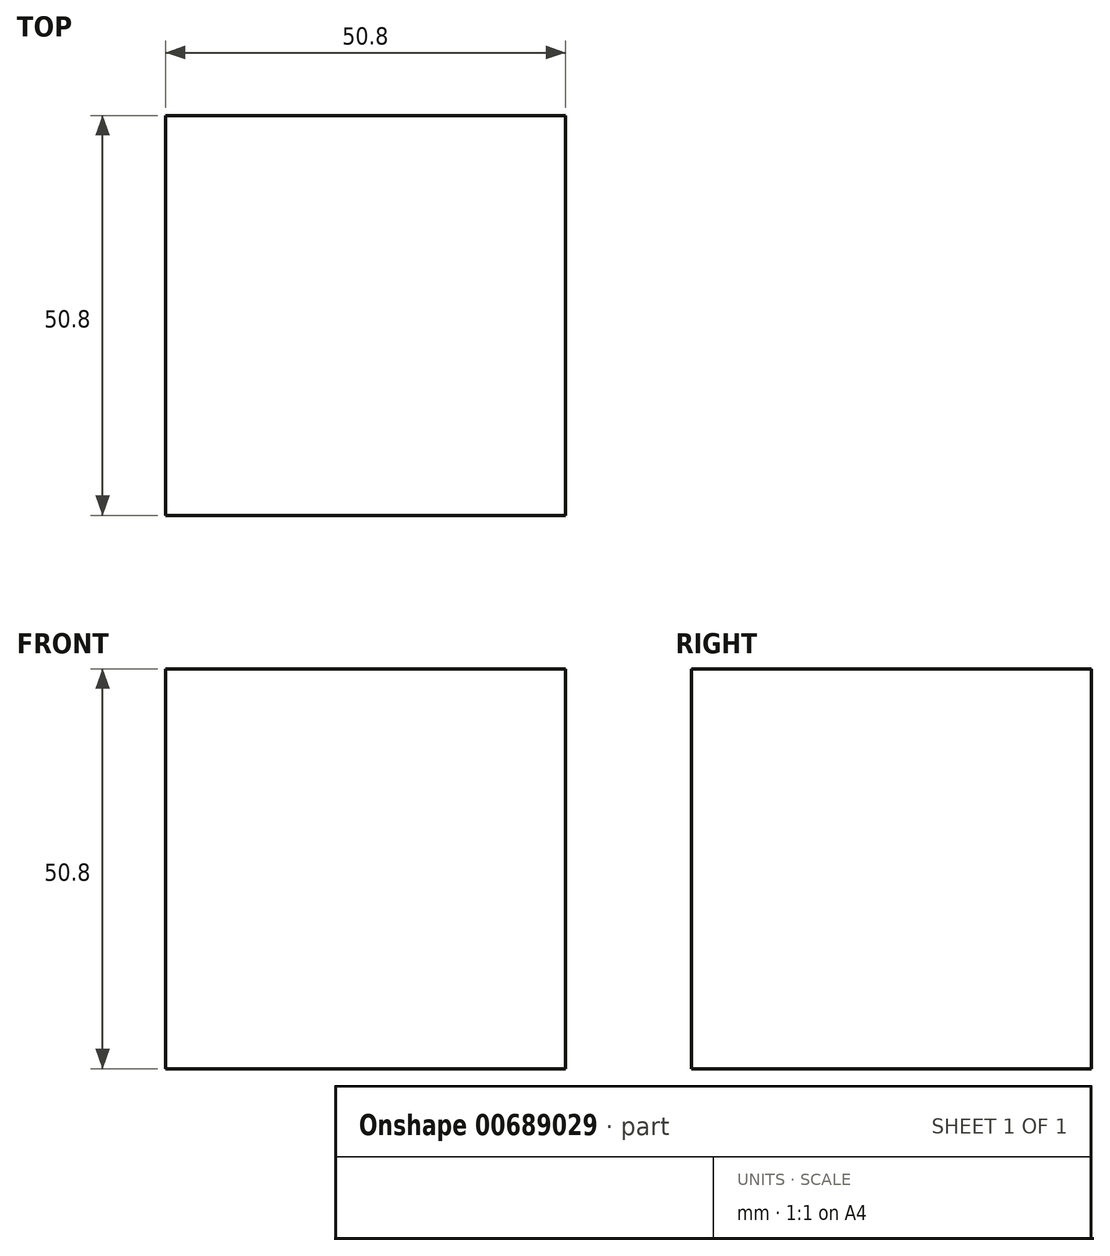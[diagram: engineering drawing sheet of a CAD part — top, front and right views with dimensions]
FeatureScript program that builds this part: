
annotation { "Feature Type Name" : "Feature", "Feature Type Description" : "" }
export const myFeature = defineFeature(function(context is Context, id is Id, definition is map)
    precondition{}
    {
        {
            var Q0;
            Q0=qCreatedBy(makeId("Front.planeOp"),FACE);
            var sketch = newSketch(context, id + "F0", { "sketchPlane" : qUnion([Q0])});
            skLineSegment(sketch, "E0", {"start": v(-61.96, 50.8) * mm, "end": v(-61.96, 0) * mm});
            skLineSegment(sketch, "E1", {"start": v(-61.96, 0) * mm, "end": v(-11.16, 0) * mm});
            skLineSegment(sketch, "E2", {"start": v(-11.16, 0) * mm, "end": v(-11.16, 50.8) * mm});
            skLineSegment(sketch, "E3", {"start": v(-11.16, 50.8) * mm, "end": v(-61.96, 50.8) * mm});
            skLineSegment(sketch, "E4", {"start": v(-61.96, 25.4) * mm, "end": v(-36.56, 25.4) * mm});
            skLineSegment(sketch, "E5", {"start": v(-36.56, 25.4) * mm, "end": v(-36.56, 0) * mm});
            skSolve(sketch);
        }
        {
            var Q0;
            {var subQ0=sQuery(id+"F0.wireOp",EDGE,"E2");Q0=makeQuery(id+"F0.imprint","IMPRINT",FACE,{"disambiguationData":[TD([[makeQuery(id+"F0.imprint","IMPRINT",EDGE,{"derivedFrom":subQ0}),1.0]])]});}
            var Q1;
            {var subQ3=sQuery(id+"F0.wireOp",EDGE,"E4");Q1=makeQuery(id+"F0.imprint","IMPRINT",FACE,{"disambiguationData":[TD([[makeQuery(id+"F0.imprint","IMPRINT",EDGE,{"derivedFrom":subQ3}),-1.0]])]});}
            extrude(context, id + "F1", {"entities" : qUnion([Q0, Q1]), "depth" : 50.8 * mm, "offsetDistance" : 25.4 * mm});
        }
    });
